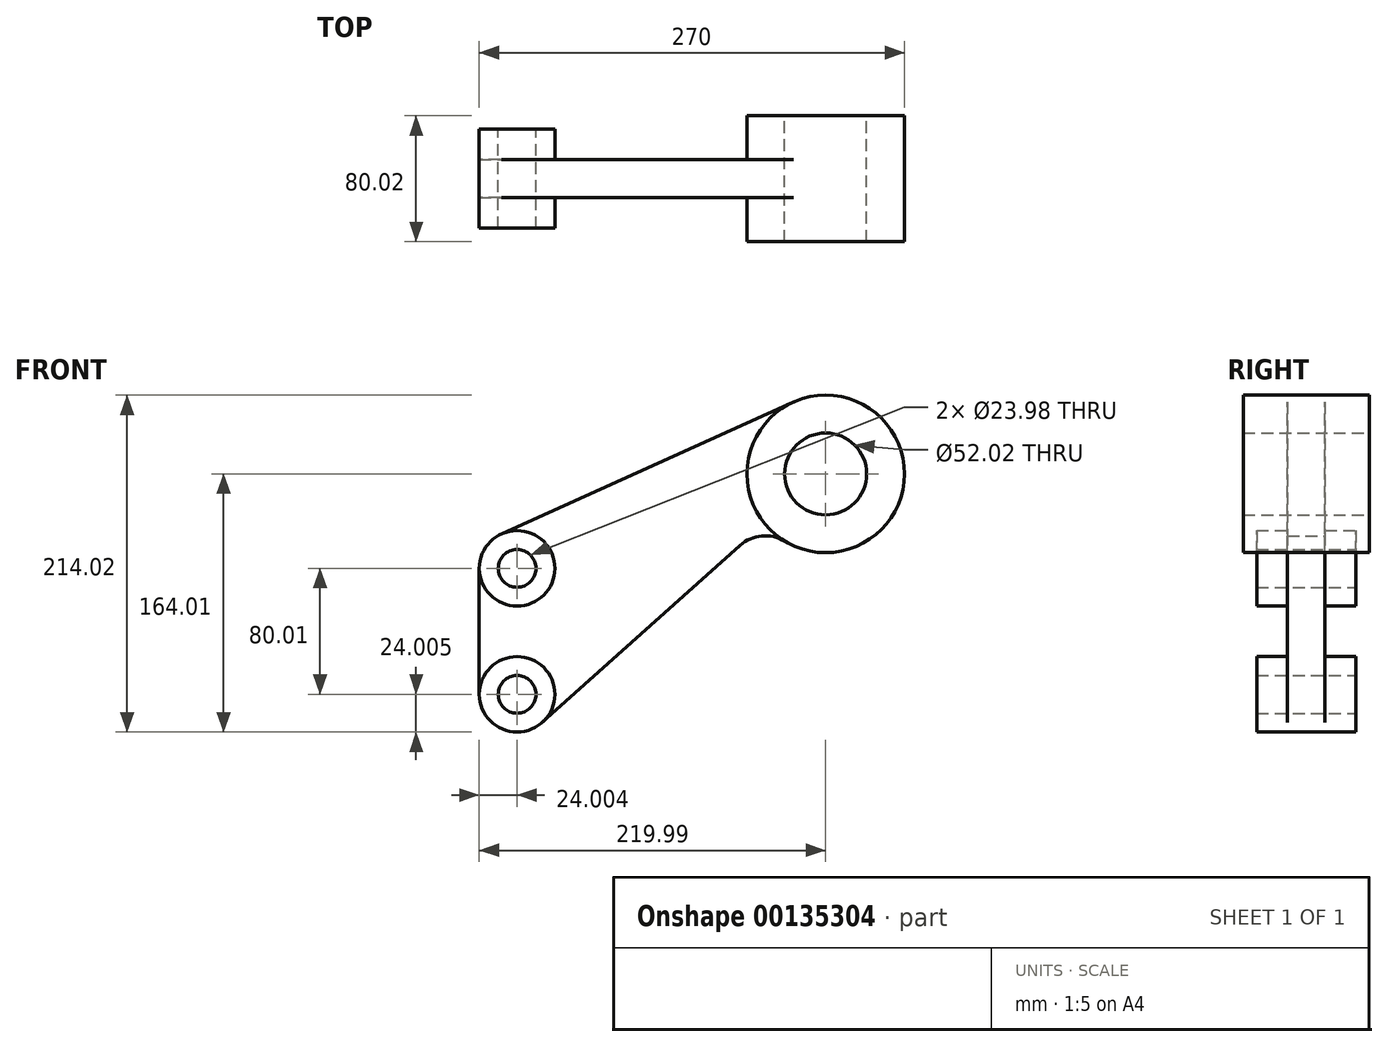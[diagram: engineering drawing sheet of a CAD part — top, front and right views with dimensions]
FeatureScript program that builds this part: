
annotation { "Feature Type Name" : "Feature", "Feature Type Description" : "" }
export const myFeature = defineFeature(function(context is Context, id is Id, definition is map)
    precondition{}
    {
        {
            var Q0;
            Q0=qCreatedBy(makeId("Front.planeOp"),FACE);
            var sketch = newSketch(context, id + "F0", { "sketchPlane" : qUnion([Q0])});
            skCircle(sketch, "E0", {"center": v(0, 0) * mm, "radius": 26 * mm});
            skCircle(sketch, "E1", {"center": v(0, 0) * mm, "radius": 50.01 * mm});
            skCircle(sketch, "E2", {"center": v(-195.99, -60) * mm, "radius": 11.99 * mm});
            skCircle(sketch, "E3", {"center": v(-195.99, -60) * mm, "radius": 24 * mm});
            skCircle(sketch, "E4", {"center": v(-195.99, -140) * mm, "radius": 11.99 * mm});
            skCircle(sketch, "E5", {"center": v(-195.99, -140) * mm, "radius": 24 * mm});
            skLineSegment(sketch, "E6", {"start": v(-205.87, -38.12) * mm, "end": v(-20.59, 45.58) * mm});
            skLineSegment(sketch, "E7", {"start": v(-219.99, -60) * mm, "end": v(-219.99, -140) * mm});
            skLineSegment(sketch, "E8", {"start": v(-179.98, -157.9) * mm, "end": v(-54.3, -45.43) * mm});
            skArc(sketch, "E9", {"start": v(-54.3, -45.43) * mm, "mid": v(-40.54, -39.42) * mm, "end": v(-25.9, -42.78) * mm});
            skSolve(sketch);
        }
        {
            var Q0;
            Q0=makeQuery(id+"F0.imprint","IMPRINT",FACE,{"disambiguationData":[TD([[makeQuery(id+"F0.imprint","IMPRINT",EDGE,{"derivedFrom":sQuery(id+"F0.wireOp",EDGE,"E0")}),-1.0]])]});
            extrude(context, id + "F1", {"entities" : qUnion([Q0]), "endBound" : BoundingType.SYMMETRIC, "depth" : 80 * mm});
        }
        {
            var Q0;
            Q0=makeQuery(id+"F0.imprint","IMPRINT",FACE,{"disambiguationData":[TD([[makeQuery(id+"F0.imprint","IMPRINT",EDGE,{"derivedFrom":sQuery(id+"F0.wireOp",EDGE,"E4")}),-1.0]])]});
            var Q1;
            Q1=makeQuery(id+"F0.imprint","IMPRINT",FACE,{"disambiguationData":[TD([[makeQuery(id+"F0.imprint","IMPRINT",EDGE,{"derivedFrom":sQuery(id+"F0.wireOp",EDGE,"E2")}),-1.0]])]});
            extrude(context, id + "F2", {"entities" : qUnion([Q0, Q1]), "operationType" : NewBodyOperationType.ADD, "endBound" : BoundingType.SYMMETRIC, "depth" : 63 * mm});
        }
        {
            var Q0;
            {var subQ0=sQuery(id+"F0.wireOp",EDGE,"E6");Q0=makeQuery(id+"F0.imprint","IMPRINT",FACE,{"disambiguationData":[TD([[makeQuery(id+"F0.imprint","IMPRINT",EDGE,{"derivedFrom":subQ0}),-1.0]])]});}
            extrude(context, id + "F3", {"entities" : qUnion([Q0]), "operationType" : NewBodyOperationType.ADD, "endBound" : BoundingType.SYMMETRIC, "depth" : 23.98 * mm});
        }
    });
